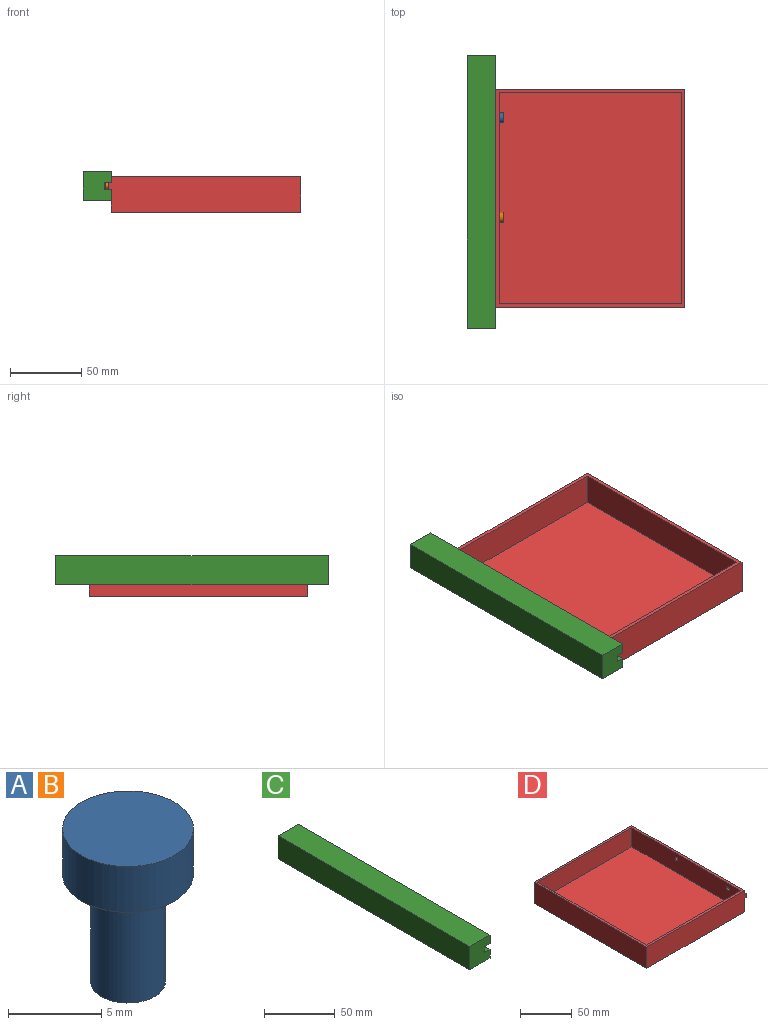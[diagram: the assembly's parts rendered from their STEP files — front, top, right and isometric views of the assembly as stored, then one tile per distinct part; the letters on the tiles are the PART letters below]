
ASSEMBLY  parts=4 mates=4
PART A: 5 faces, bbox 7x7x10 mm
  f0: plane 4x4mm, normal (0,0,-1), area 12.6mm2, adj f1
  f1: cylinder r=2mm len=7mm, axis (0,0,-1), area 88mm2, adj f0,f2
  f2: plane 7x7mm, normal (0,0,-1), area 25.9mm2, adj f1,f3
  f3: cylinder r=3.5mm len=7mm, axis (0,0,-1), area 66mm2, adj f2,f4
  f4: plane 7x7mm, normal (0,0,1), area 38.5mm2, adj f3
PART B: same geometry as A
PART C: 10 faces, bbox 20x191.2x20 mm
  f0: plane 191.2x5mm, normal (0,0,-1), area 956mm2, adj f1,f7,f8,f9
  f1: plane 191.2x7.5mm, normal (1,0,0), area 1434mm2, adj f0,f2,f8,f9
  f2: plane 191.2x20mm, normal (0,0,1), area 3824mm2, adj f1,f3,f8,f9
  f3: plane 191.2x20mm, normal (-1,0,0), area 3824mm2, adj f2,f4,f8,f9
  f4: plane 191.2x20mm, normal (0,0,-1), area 3824mm2, adj f3,f5,f8,f9
  f5: plane 191.2x7.5mm, normal (1,0,0), area 1434mm2, adj f4,f6,f8,f9
  f6: plane 191.2x5mm, normal (0,0,1), area 956mm2, adj f5,f7,f8,f9
  f7: plane 191.2x5mm, normal (1,0,0), area 956mm2, adj f0,f6,f8,f9
  f8: plane 20x20mm, normal (0,-1,0), area 375mm2, adj f0,f1,f2,f3,f4,f5,f6,f7
  f9: plane 20x20mm, normal (0,1,0), area 375mm2, adj f0,f1,f2,f3,f4,f5,f6,f7
PART D: 17 faces, bbox 135.1x153.3x25 mm
  f0: plane 153.27x16.1mm, normal (1,0,0), area 2467.7mm2, adj f2,f4,f6,f13
  f1: plane 153.27x133.13mm, normal (0,0,1), area 1407mm2, adj f2,f3,f4,f5,f7,f8,f9,f10
  f2: plane 135.13x25mm, normal (0,1,0), area 3338.1mm2, adj f0,f1,f3,f5,f6,f12,f13,f14
  f3: plane 153.27x25mm, normal (-1,0,0), area 3831.9mm2, adj f1,f2,f4,f6
  f4: plane 135.13x25mm, normal (0,-1,0), area 3338.1mm2, adj f0,f1,f3,f5,f6,f12,f13,f14
  f5: plane 153.27x4mm, normal (1,0,0), area 613.1mm2, adj f1,f2,f4,f12
  f6: plane 153.27x133.13mm, normal (0,0,-1), area 20406mm2, adj f0,f2,f3,f4
  f7: plane 128.13x22.5mm, normal (0,-1,0), area 2883mm2, adj f1,f8,f10,f11
  f8: plane 148.27x22.5mm, normal (1,0,0), area 3336.2mm2, adj f1,f7,f9,f11
  f9: plane 128.13x22.5mm, normal (0,1,0), area 2883mm2, adj f1,f8,f10,f11
  f10: plane 148.27x22.5mm, normal (-1,0,0), area 3311mm2, adj f1,f7,f9,f11,f15,f16
  f11: plane 148.27x128.13mm, normal (0,0,1), area 18999mm2, adj f7,f8,f9,f10
  f12: plane 153.27x2mm, normal (0,0,1), area 306.5mm2, adj f2,f4,f5,f14
  f13: plane 153.27x2mm, normal (0,0,-1), area 306.5mm2, adj f0,f2,f4,f14
  f14: plane 153.27x4.9mm, normal (1,0,0), area 725.9mm2, adj f2,f4,f12,f13,f15,f16
  f15: cylinder r=2mm len=4.5mm, axis (-1,0,0), area 56.5mm2, adj f10,f14
  f16: cylinder r=2mm len=4.5mm, axis (-1,0,0), area 56.5mm2, adj f10,f14
PLACE A rot(axis=(0,1,0),90deg) t=(-42.42,8.63,-23.71)mm
PLACE B rot(axis=(0,1,0),90deg) t=(-42.42,-61.37,-23.71)mm
PLACE C t=(-57.92,52.1,-33.76)mm fixed
PLACE D rot(axis=(0,0,1),180deg) t=(95.22,-124.64,-42.26)mm
MATE planar C.f0 <-> D.f12  axis (0,0,-1) through (-40.42,-43.5,-21.26)mm
MATE fastened B.f1 <-> D.f15  axis (-1,0,0) through (-35.42,-61.37,-23.71)mm
MATE planar D.f0 <-> C.f5  axis (-1,0,0) through (-37.92,-48,-34.21)mm
MATE fastened A.f1 <-> D.f16  axis (-1,0,0) through (-35.42,8.63,-23.71)mm
